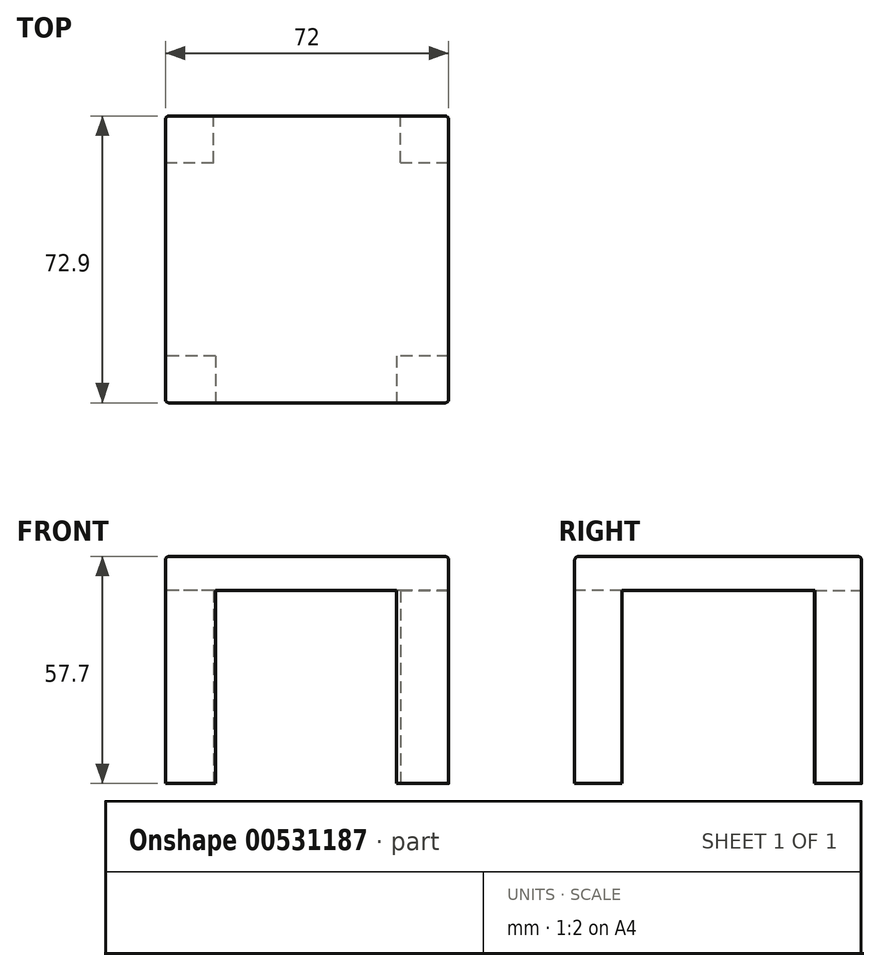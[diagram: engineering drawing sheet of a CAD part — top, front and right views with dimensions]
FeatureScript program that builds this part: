
annotation { "Feature Type Name" : "Feature", "Feature Type Description" : "" }
export const myFeature = defineFeature(function(context is Context, id is Id, definition is map)
    precondition{}
    {
        {
            var Q0;
            Q0=qCreatedBy(makeId("Top.planeOp"),FACE);
            var sketch = newSketch(context, id + "F0", { "sketchPlane" : qUnion([Q0])});
            skLineSegment(sketch, "E0.bottom", {"start": v(36, 36.45) * mm, "end": v(-36, 36.45) * mm});
            skLineSegment(sketch, "E0.top", {"start": v(36, -36.45) * mm, "end": v(-36, -36.45) * mm});
            skLineSegment(sketch, "E0.left", {"start": v(36, 36.45) * mm, "end": v(36, -36.45) * mm});
            skLineSegment(sketch, "E0.right", {"start": v(-36, 36.45) * mm, "end": v(-36, -36.45) * mm});
            skPoint(sketch, "E0.middle", {"position": v(0, 0) * mm});
            skSolve(sketch);
        }
        {
            var Q0;
            Q0 = qSketchRegion(id + "F0", true);
            extrude(context, id + "F1", {"entities" : qUnion([Q0]), "depth" : 57.7 * mm, "offsetDistance" : 25 * mm});
        }
        {
            var Q0;
            Q0=makeQuery(id+"F1.opExtrude","CAP_FACE",FACE,{"disambiguationData":[OSD([sQuery(id+"F0.wireOp",EDGE,"E0.bottom"),sQuery(id+"F0.wireOp",EDGE,"E0.top"),sQuery(id+"F0.wireOp",EDGE,"E0.left"),sQuery(id+"F0.wireOp",EDGE,"E0.right")])],"isStart":true});
            var sketch = newSketch(context, id + "F2", { "sketchPlane" : qUnion([Q0])});
            skLineSegment(sketch, "E1.bottom", {"start": v(23.7, 24.5) * mm, "end": v(-23.7, 24.5) * mm});
            skLineSegment(sketch, "E1.top", {"start": v(23.7, -24.5) * mm, "end": v(-23.7, -24.5) * mm});
            skLineSegment(sketch, "E1.left", {"start": v(23.7, 24.5) * mm, "end": v(23.7, -24.5) * mm});
            skLineSegment(sketch, "E1.right", {"start": v(-23.7, 24.5) * mm, "end": v(-23.7, -24.5) * mm});
            skPoint(sketch, "E1.middle", {"position": v(0, 0) * mm});
            skSolve(sketch);
        }
        {
            var Q0;
            Q0 = qSketchRegion(id + "F2", true);
            extrude(context, id + "F3", {"entities" : qUnion([Q0]), "operationType" : NewBodyOperationType.REMOVE, "oppositeDirection" : true, "depth" : 49 * mm, "offsetDistance" : 25 * mm});
        }
        {
            var Q0;
            Q0=makeQuery(id+"F1.opExtrude","CAP_FACE",FACE,{"disambiguationData":[OSD([sQuery(id+"F0.wireOp",EDGE,"E0.bottom"),sQuery(id+"F0.wireOp",EDGE,"E0.top"),sQuery(id+"F0.wireOp",EDGE,"E0.left"),sQuery(id+"F0.wireOp",EDGE,"E0.right")])],"isStart":true});
            var sketch = newSketch(context, id + "F4", { "sketchPlane" : qUnion([Q0])});
            skLineSegment(sketch, "E2.bottom", {"start": v(-23.7, 24.5) * mm, "end": v(23.7, 24.5) * mm});
            skLineSegment(sketch, "E2.top", {"start": v(-23.7, 36.45) * mm, "end": v(23.7, 36.45) * mm});
            skLineSegment(sketch, "E2.left", {"start": v(-23.7, 24.5) * mm, "end": v(-23.7, 36.45) * mm});
            skLineSegment(sketch, "E2.right", {"start": v(23.7, 24.5) * mm, "end": v(23.7, 36.45) * mm});
            skLineSegment(sketch, "E3.bottom", {"start": v(-23.7, -24.5) * mm, "end": v(23.7, -24.5) * mm});
            skLineSegment(sketch, "E3.top", {"start": v(-23.7, -36.45) * mm, "end": v(23.7, -36.45) * mm});
            skLineSegment(sketch, "E3.left", {"start": v(-23.7, -24.5) * mm, "end": v(-23.7, -36.45) * mm});
            skLineSegment(sketch, "E3.right", {"start": v(23.7, -24.5) * mm, "end": v(23.7, -36.45) * mm});
            skLineSegment(sketch, "E4.bottom", {"start": v(23.7, 24.5) * mm, "end": v(36, 24.5) * mm});
            skLineSegment(sketch, "E4.top", {"start": v(23.7, -24.5) * mm, "end": v(36, -24.5) * mm});
            skLineSegment(sketch, "E4.left", {"start": v(23.7, 24.5) * mm, "end": v(23.7, -24.5) * mm});
            skLineSegment(sketch, "E4.right", {"start": v(36, 24.5) * mm, "end": v(36, -24.5) * mm});
            skLineSegment(sketch, "E5.bottom", {"start": v(-23.7, 24.5) * mm, "end": v(-36, 24.5) * mm});
            skLineSegment(sketch, "E5.top", {"start": v(-23.7, -24.5) * mm, "end": v(-36, -24.5) * mm});
            skLineSegment(sketch, "E5.left", {"start": v(-23.7, 24.5) * mm, "end": v(-23.7, -24.5) * mm});
            skLineSegment(sketch, "E5.right", {"start": v(-36, 24.5) * mm, "end": v(-36, -24.5) * mm});
            skSolve(sketch);
        }
        {
            var Q0;
            Q0=makeQuery(id+"F4.imprint","IMPRINT",FACE,{"disambiguationData":[TD([[makeQuery(id+"F4.imprint","IMPRINT",EDGE,{"derivedFrom":sQuery(id+"F4.wireOp",EDGE,"E5.bottom")}),1.0]])]});
            extrude(context, id + "F5", {"entities" : qUnion([Q0]), "operationType" : NewBodyOperationType.REMOVE, "oppositeDirection" : true, "depth" : 49 * mm, "offsetDistance" : 25 * mm});
        }
        {
            var Q0;
            Q0=makeQuery(id+"F1.opExtrude","CAP_FACE",FACE,{"disambiguationData":[OSD([sQuery(id+"F0.wireOp",EDGE,"E0.bottom"),sQuery(id+"F0.wireOp",EDGE,"E0.top"),sQuery(id+"F0.wireOp",EDGE,"E0.left"),sQuery(id+"F0.wireOp",EDGE,"E0.right")])],"isStart":true});
            var sketch = newSketch(context, id + "F6", { "sketchPlane" : qUnion([Q0])});
            skLineSegment(sketch, "E6.bottom", {"start": v(23.7, 24.5) * mm, "end": v(36, 24.5) * mm});
            skLineSegment(sketch, "E6.top", {"start": v(23.7, -24.57) * mm, "end": v(36, -24.57) * mm});
            skLineSegment(sketch, "E6.left", {"start": v(23.7, 24.5) * mm, "end": v(23.7, -24.57) * mm});
            skLineSegment(sketch, "E6.right", {"start": v(36, 24.5) * mm, "end": v(36, -24.57) * mm});
            skSolve(sketch);
        }
        {
            var Q0;
            Q0 = qSketchRegion(id + "F6", true);
            extrude(context, id + "F7", {"entities" : qUnion([Q0]), "operationType" : NewBodyOperationType.REMOVE, "oppositeDirection" : true, "depth" : 49 * mm, "offsetDistance" : 25 * mm});
        }
        {
            var Q0;
            {var subQ0=sQuery(id+"F0.wireOp",EDGE,"E0.left");var subQ1=sQuery(id+"F0.wireOp",EDGE,"E0.right");var subQ2=sQuery(id+"F0.wireOp",EDGE,"E0.bottom");Q0=makeQuery(id+"F7.boolean.opBoolean","SPLIT",FACE,{"disambiguationData":[TD([makeQuery(id+"F1.opExtrude","SWEPT_FACE",FACE,{"disambiguationData":[OSD([subQ2])]})])],"derivedFrom":makeQuery(id+"F1.opExtrude","CAP_FACE",FACE,{"disambiguationData":[OSD([subQ2,sQuery(id+"F0.wireOp",EDGE,"E0.top"),subQ0,subQ1])],"isStart":true})});}
            var sketch = newSketch(context, id + "F8", { "sketchPlane" : qUnion([Q0])});
            skLineSegment(sketch, "E7.bottom", {"start": v(23.7, -24.5) * mm, "end": v(-23.8, -24.5) * mm});
            skLineSegment(sketch, "E7.top", {"start": v(23.7, -36.45) * mm, "end": v(-23.8, -36.45) * mm});
            skLineSegment(sketch, "E7.left", {"start": v(23.7, -24.5) * mm, "end": v(23.7, -36.45) * mm});
            skLineSegment(sketch, "E7.right", {"start": v(-23.8, -24.5) * mm, "end": v(-23.8, -36.45) * mm});
            skSolve(sketch);
        }
        {
            var Q0;
            Q0 = qSketchRegion(id + "F8", true);
            extrude(context, id + "F9", {"entities" : qUnion([Q0]), "operationType" : NewBodyOperationType.REMOVE, "oppositeDirection" : true, "depth" : 49 * mm, "offsetDistance" : 25 * mm});
        }
        {
            var Q0;
            {var subQ0=sQuery(id+"F0.wireOp",EDGE,"E0.right");var subQ1=sQuery(id+"F0.wireOp",EDGE,"E0.left");var subQ2=sQuery(id+"F0.wireOp",EDGE,"E0.top");Q0=makeQuery(id+"F7.boolean.opBoolean","SPLIT",FACE,{"disambiguationData":[TD([makeQuery(id+"F1.opExtrude","SWEPT_FACE",FACE,{"disambiguationData":[OSD([subQ2])]})])],"derivedFrom":makeQuery(id+"F1.opExtrude","CAP_FACE",FACE,{"disambiguationData":[OSD([sQuery(id+"F0.wireOp",EDGE,"E0.bottom"),subQ2,subQ1,subQ0])],"isStart":true})});}
            var sketch = newSketch(context, id + "F10", { "sketchPlane" : qUnion([Q0])});
            skLineSegment(sketch, "E8.bottom", {"start": v(22.76, 24.5) * mm, "end": v(-23.27, 24.5) * mm});
            skLineSegment(sketch, "E8.top", {"start": v(22.76, 36.45) * mm, "end": v(-23.27, 36.45) * mm});
            skLineSegment(sketch, "E8.left", {"start": v(22.76, 24.5) * mm, "end": v(22.76, 36.45) * mm});
            skLineSegment(sketch, "E8.right", {"start": v(-23.27, 24.5) * mm, "end": v(-23.27, 36.45) * mm});
            skSolve(sketch);
        }
        {
            var Q0;
            Q0 = qSketchRegion(id + "F10", true);
            extrude(context, id + "F11", {"entities" : qUnion([Q0]), "operationType" : NewBodyOperationType.REMOVE, "oppositeDirection" : true, "depth" : 49 * mm, "offsetDistance" : 25 * mm});
        }
        {
            var Q0;
            Q0=makeQuery(id+"F1.opExtrude","CAP_EDGE",EDGE,{"disambiguationData":[OSD([sQuery(id+"F0.wireOp",EDGE,"E0.top")])],"isStart":false});
            fillet(context, id + "F12", {"entities" : qUnion([Q0]), "radius" : 1 * mm, "tangentPropagation" : true, "allowEdgeOverflow" : false});
        }
        {
            var Q0;
            Q0=makeQuery(id+"F1.opExtrude","CAP_EDGE",EDGE,{"disambiguationData":[OSD([sQuery(id+"F0.wireOp",EDGE,"E0.right")])],"isStart":false});
            fillet(context, id + "F13", {"entities" : qUnion([Q0]), "radius" : 1 * mm, "tangentPropagation" : true, "allowEdgeOverflow" : false});
        }
        {
            var Q0;
            Q0=makeQuery(id+"F1.opExtrude","CAP_EDGE",EDGE,{"disambiguationData":[OSD([sQuery(id+"F0.wireOp",EDGE,"E0.bottom")])],"isStart":false});
            fillet(context, id + "F14", {"entities" : qUnion([Q0]), "radius" : 1 * mm, "tangentPropagation" : true, "allowEdgeOverflow" : false});
        }
        {
            var Q0;
            Q0=makeQuery(id+"F1.opExtrude","CAP_EDGE",EDGE,{"disambiguationData":[OSD([sQuery(id+"F0.wireOp",EDGE,"E0.left")])],"isStart":false});
            fillet(context, id + "F15", {"entities" : qUnion([Q0]), "radius" : 1 * mm, "tangentPropagation" : true, "allowEdgeOverflow" : false});
        }
    });
